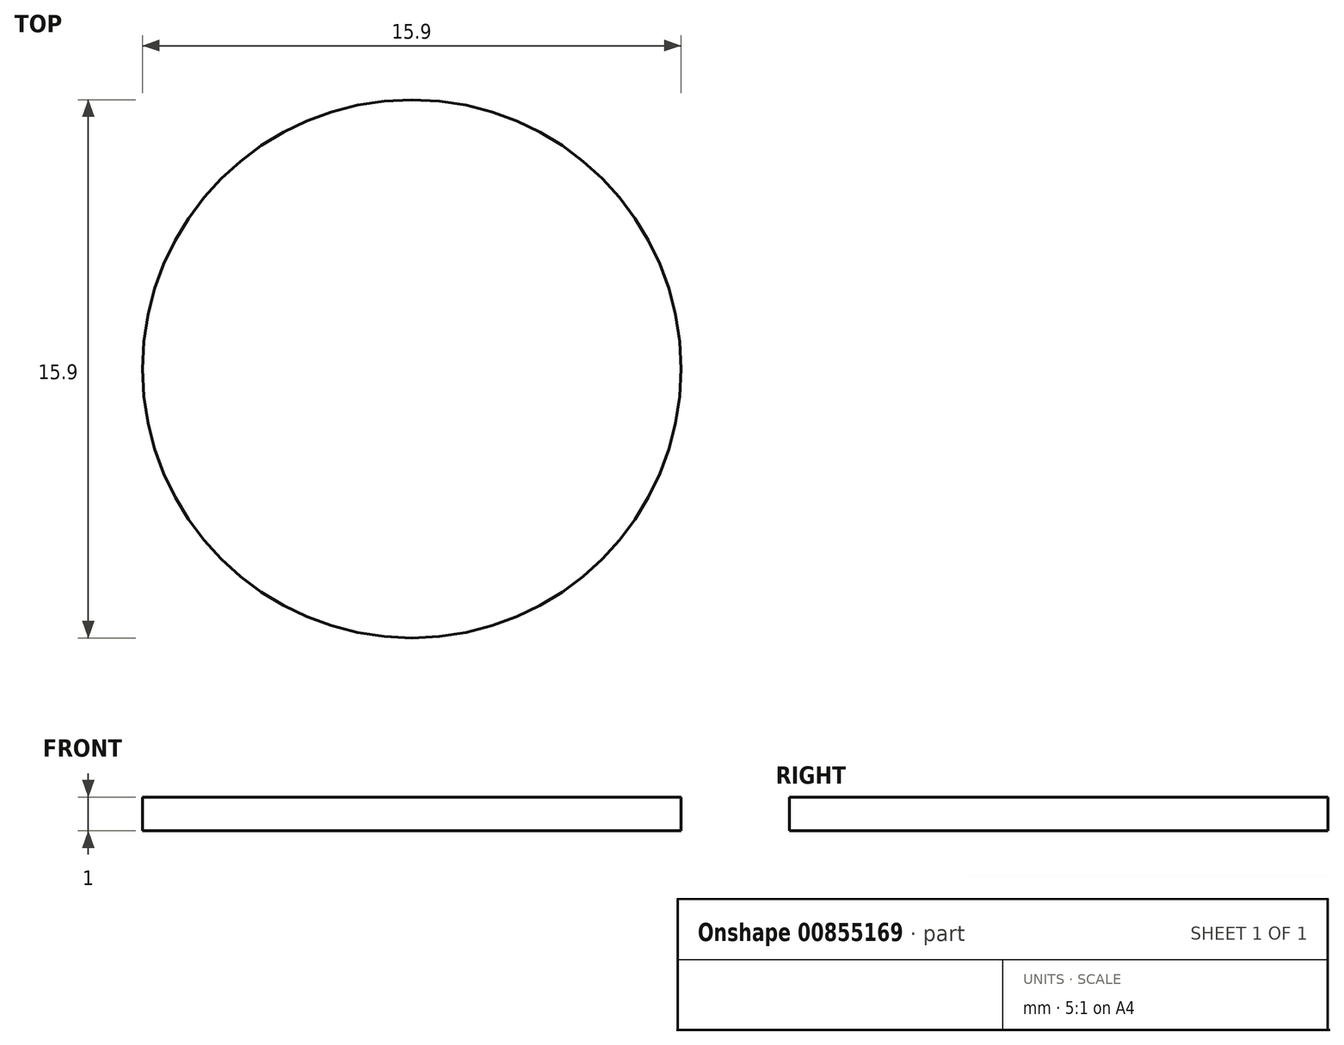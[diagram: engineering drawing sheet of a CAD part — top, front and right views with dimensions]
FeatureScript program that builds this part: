
annotation { "Feature Type Name" : "Feature", "Feature Type Description" : "" }
export const myFeature = defineFeature(function(context is Context, id is Id, definition is map)
    precondition{}
    {
        {
            var Q0;
            Q0=qCreatedBy(makeId("Top.planeOp"),FACE);
            var sketch = newSketch(context, id + "F0", { "sketchPlane" : qUnion([Q0])});
            skCircle(sketch, "E0", {"center": v(0, 0) * mm, "radius": 7.95 * mm});
            skSolve(sketch);
        }
        {
            var Q0;
            Q0=makeQuery(id+"F0.imprint","IMPRINT",FACE,{"disambiguationData":[TD([[makeQuery(id+"F0.imprint","IMPRINT",EDGE,{"derivedFrom":sQuery(id+"F0.wireOp",EDGE,"E0")}),1.0]])]});
            extrude(context, id + "F1", {"entities" : qUnion([Q0]), "depth" : 1 * mm, "offsetDistance" : 25 * mm});
        }
    });
